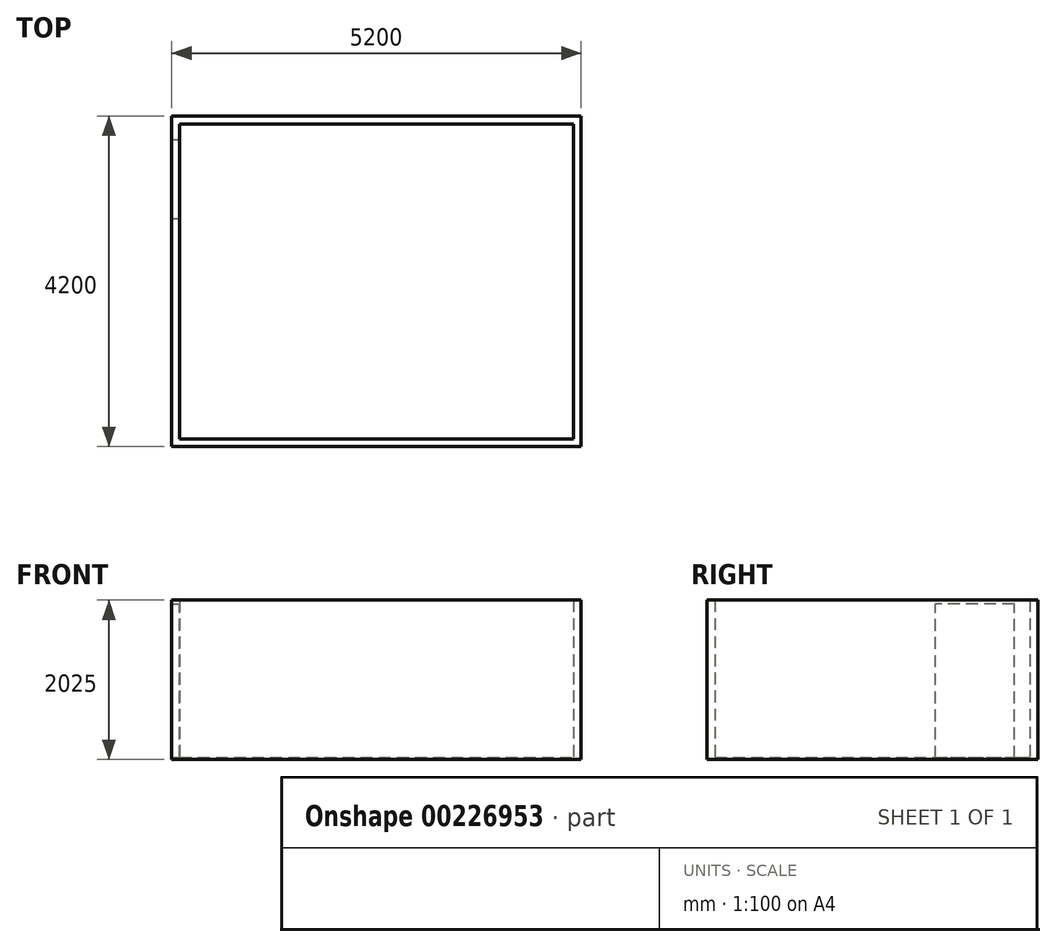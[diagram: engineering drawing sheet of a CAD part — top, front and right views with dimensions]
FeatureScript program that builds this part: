
annotation { "Feature Type Name" : "Feature", "Feature Type Description" : "" }
export const myFeature = defineFeature(function(context is Context, id is Id, definition is map)
    precondition{}
    {
        {
            var Q0;
            Q0=qCreatedBy(makeId("Top.planeOp"),FACE);
            var sketch = newSketch(context, id + "F0", { "sketchPlane" : qUnion([Q0])});
            skLineSegment(sketch, "E0.bottom", {"start": v(-2500, -2000) * mm, "end": v(2500, -2000) * mm});
            skLineSegment(sketch, "E0.top", {"start": v(-2500, 2000) * mm, "end": v(2500, 2000) * mm});
            skLineSegment(sketch, "E0.left", {"start": v(-2500, -2000) * mm, "end": v(-2500, 2000) * mm});
            skLineSegment(sketch, "E0.right", {"start": v(2500, -2000) * mm, "end": v(2500, 2000) * mm});
            skPoint(sketch, "E0.middle", {"position": v(0, 0) * mm});
            skLineSegment(sketch, "E1.bottom", {"start": v(2600, 2100) * mm, "end": v(-2600, 2100) * mm});
            skLineSegment(sketch, "E1.top", {"start": v(2600, -2100) * mm, "end": v(-2600, -2100) * mm});
            skLineSegment(sketch, "E1.left", {"start": v(2600, 2100) * mm, "end": v(2600, -2100) * mm});
            skLineSegment(sketch, "E1.right", {"start": v(-2600, 2100) * mm, "end": v(-2600, -2100) * mm});
            skSolve(sketch);
        }
        {
            var Q0;
            Q0=makeQuery(id+"F0.imprint","IMPRINT",FACE,{"disambiguationData":[TD([[makeQuery(id+"F0.imprint","IMPRINT",EDGE,{"derivedFrom":sQuery(id+"F0.wireOp",EDGE,"E0.bottom")}),-1.0]])]});
            extrude(context, id + "F1", {"entities" : qUnion([Q0]), "depth" : 2000 * mm});
        }
        {
            var Q0;
            Q0=makeQuery(id+"F1.opExtrude","CAP_FACE",FACE,{"disambiguationData":[OSD([sQuery(id+"F0.wireOp",EDGE,"E0.bottom"),sQuery(id+"F0.wireOp",EDGE,"E0.top"),sQuery(id+"F0.wireOp",EDGE,"E0.left"),sQuery(id+"F0.wireOp",EDGE,"E0.right"),sQuery(id+"F0.wireOp",EDGE,"E1.bottom"),sQuery(id+"F0.wireOp",EDGE,"E1.top"),sQuery(id+"F0.wireOp",EDGE,"E1.left"),sQuery(id+"F0.wireOp",EDGE,"E1.right")])],"isStart":true});
            var sketch = newSketch(context, id + "F2", { "sketchPlane" : qUnion([Q0])});
            skSolve(sketch);
        }
        {
            var Q0;
            Q0=makeQuery(id+"F2.imprint","IMPRINT",FACE,{"disambiguationData":[TD([[makeQuery(id+"F2.imprint","IMPRINT",EDGE,{"derivedFrom":makeQuery(id+"F1.opExtrude","CAP_EDGE",EDGE,{"disambiguationData":[OSD([sQuery(id+"F0.wireOp",EDGE,"E0.bottom")])],"isStart":true})}),1.0]])]});
            var Q1;
            Q1=makeQuery(id+"F2.imprint","IMPRINT",FACE,{"disambiguationData":[TD([[makeQuery(id+"F2.imprint","IMPRINT",EDGE,{"derivedFrom":makeQuery(id+"F1.opExtrude","CAP_EDGE",EDGE,{"disambiguationData":[OSD([sQuery(id+"F0.wireOp",EDGE,"E0.bottom")])],"isStart":true})}),-1.0]])]});
            extrude(context, id + "F3", {"entities" : qUnion([Q0, Q1]), "operationType" : NewBodyOperationType.ADD, "depth" : 25 * mm});
        }
        {
            var Q0;
            Q0=makeQuery(id+"F1.opExtrude","SWEPT_FACE",FACE,{"disambiguationData":[OSD([sQuery(id+"F0.wireOp",EDGE,"E0.left")])]});
            var sketch = newSketch(context, id + "F4", { "sketchPlane" : qUnion([Q0])});
            skLineSegment(sketch, "E2.bottom", {"start": v(1800, 0) * mm, "end": v(800, 0) * mm});
            skLineSegment(sketch, "E2.top", {"start": v(1800, 1950) * mm, "end": v(800, 1950) * mm});
            skLineSegment(sketch, "E2.left", {"start": v(1800, 0) * mm, "end": v(1800, 1950) * mm});
            skLineSegment(sketch, "E2.right", {"start": v(800, 0) * mm, "end": v(800, 1950) * mm});
            skSolve(sketch);
        }
        {
            var Q0;
            Q0=makeQuery(id+"F4.imprint","IMPRINT",FACE,{"disambiguationData":[TD([[makeQuery(id+"F4.imprint","IMPRINT",EDGE,{"derivedFrom":sQuery(id+"F4.wireOp",EDGE,"E2.bottom")}),1.0]])]});
            extrude(context, id + "F5", {"entities" : qUnion([Q0]), "operationType" : NewBodyOperationType.REMOVE, "oppositeDirection" : true, "depth" : 200 * mm});
        }
    });
